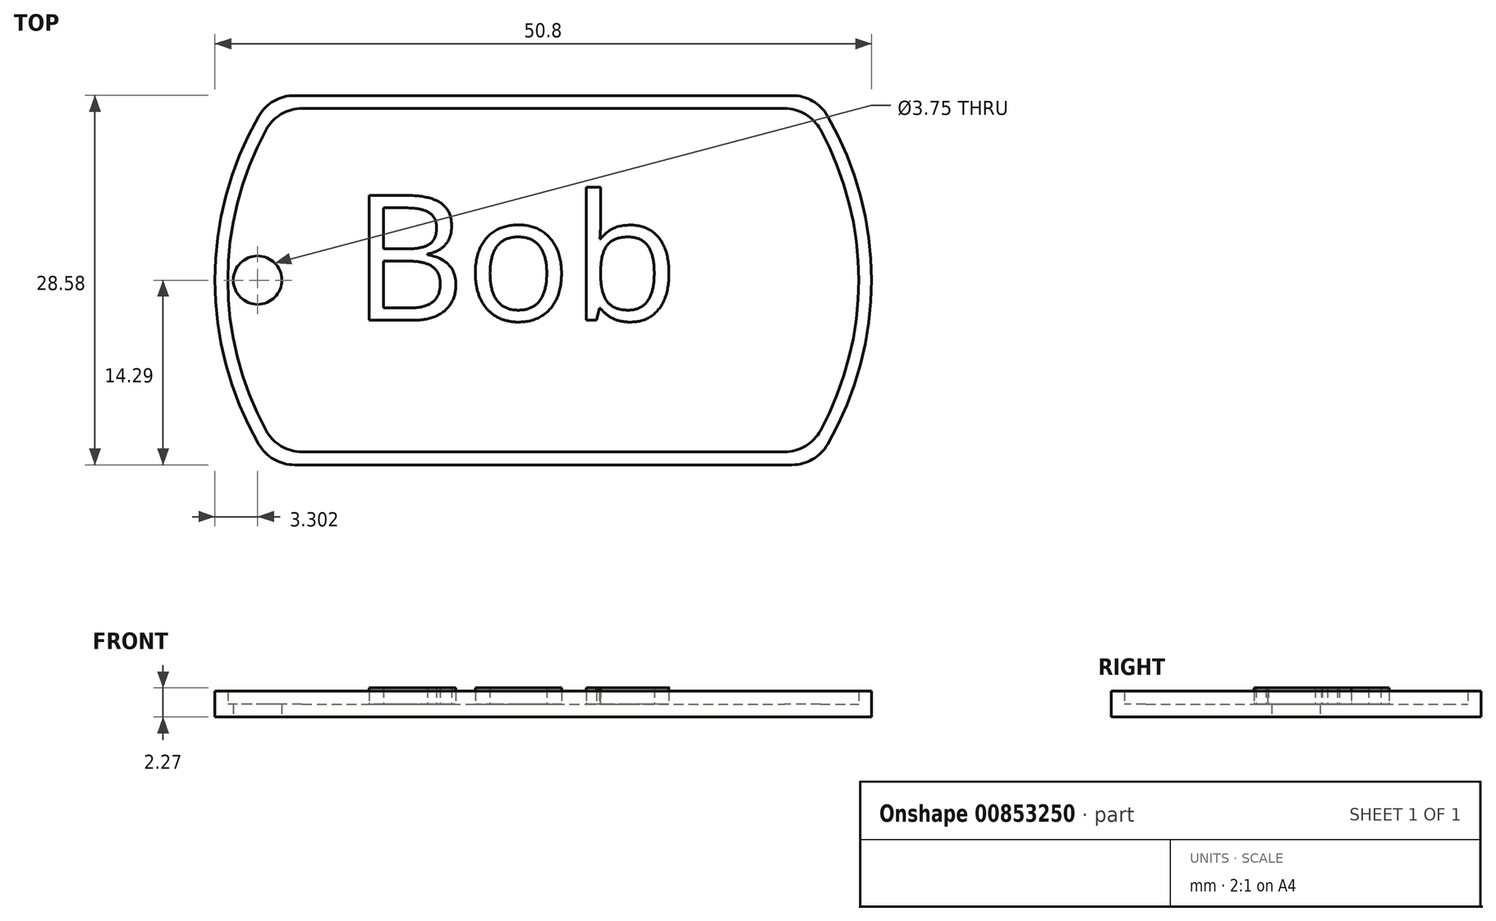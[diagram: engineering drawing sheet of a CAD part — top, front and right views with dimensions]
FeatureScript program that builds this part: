
annotation { "Feature Type Name" : "Feature", "Feature Type Description" : "" }
export const myFeature = defineFeature(function(context is Context, id is Id, definition is map)
    precondition{}
    {
        {
            var Q0;
            Q0=qCreatedBy(makeId("Top.planeOp"),FACE);
            var sketch = newSketch(context, id + "F0", { "sketchPlane" : qUnion([Q0])});
            skArc(sketch, "E0", {"start": v(-22, 12.7) * mm, "mid": v(-25.4, 0) * mm, "end": v(-22, -12.7) * mm});
            skLineSegment(sketch, "E1.top", {"start": v(-19.25, -14.29) * mm, "end": v(19.25, -14.29) * mm});
            skArc(sketch, "E2.trimOffspring", {"start": v(22, -12.7) * mm, "mid": v(25.4, 0) * mm, "end": v(22, 12.7) * mm});
            skLineSegment(sketch, "E3", {"start": v(-19.25, 14.29) * mm, "end": v(19.25, 14.29) * mm});
            skPoint(sketch, "E4.visualSharp", {"position": v(-21, 14.29) * mm});
            skArc(sketch, "E4.filletArc", {"start": v(-19.25, 14.29) * mm, "mid": v(-20.83, 13.86) * mm, "end": v(-22, 12.7) * mm});
            skPoint(sketch, "E5.visualSharp", {"position": v(21, 14.29) * mm});
            skArc(sketch, "E5.filletArc", {"start": v(22, 12.7) * mm, "mid": v(20.83, 13.86) * mm, "end": v(19.25, 14.29) * mm});
            skPoint(sketch, "E6.visualSharp", {"position": v(21, -14.29) * mm});
            skArc(sketch, "E6.filletArc", {"start": v(19.25, -14.29) * mm, "mid": v(20.83, -13.86) * mm, "end": v(22, -12.7) * mm});
            skPoint(sketch, "E7.visualSharp", {"position": v(-21, -14.29) * mm});
            skArc(sketch, "E7.filletArc", {"start": v(-22, -12.7) * mm, "mid": v(-20.83, -13.86) * mm, "end": v(-19.25, -14.29) * mm});
            skCircle(sketch, "E8", {"center": v(-22.1, 0) * mm, "radius": 1.87 * mm});
            skSolve(sketch);
        }
        {
            var Q0;
            Q0=makeQuery(id+"F0.imprint","IMPRINT",FACE,{"disambiguationData":[TD([[makeQuery(id+"F0.imprint","IMPRINT",EDGE,{"derivedFrom":sQuery(id+"F0.wireOp",EDGE,"E0")}),1.0]])]});
            extrude(context, id + "F1", {"entities" : qUnion([Q0]), "depth" : 1 * mm, "offsetDistance" : 25.4 * mm});
        }
        {
            var Q0;
            Q0=makeQuery(id+"F1.opExtrude","CAP_FACE",FACE,{"disambiguationData":[OSD([sQuery(id+"F0.wireOp",EDGE,"E0"),sQuery(id+"F0.wireOp",EDGE,"E1.top"),sQuery(id+"F0.wireOp",EDGE,"E2.trimOffspring"),sQuery(id+"F0.wireOp",EDGE,"E3"),sQuery(id+"F0.wireOp",EDGE,"E4.filletArc"),sQuery(id+"F0.wireOp",EDGE,"E5.filletArc"),sQuery(id+"F0.wireOp",EDGE,"E6.filletArc"),sQuery(id+"F0.wireOp",EDGE,"E7.filletArc")])],"isStart":false});
            var sketch = newSketch(context, id + "F2", { "sketchPlane" : qUnion([Q0])});
            skLineSegment(sketch, "E9.0", {"start": v(-18.66, 13.29) * mm, "end": v(18.66, 13.29) * mm});
            skArc(sketch, "E9.1", {"start": v(-21.45, 11.63) * mm, "mid": v(-24.4, 0) * mm, "end": v(-21.45, -11.63) * mm});
            skLineSegment(sketch, "E9.2", {"start": v(-18.66, -13.29) * mm, "end": v(18.66, -13.29) * mm});
            skArc(sketch, "E9.3", {"start": v(21.45, -11.63) * mm, "mid": v(24.4, 0) * mm, "end": v(21.45, 11.63) * mm});
            skPoint(sketch, "E10.visualSharp", {"position": v(-20.46, 13.29) * mm});
            skArc(sketch, "E10.filletArc", {"start": v(-18.66, 13.29) * mm, "mid": v(-20.29, 12.84) * mm, "end": v(-21.45, 11.63) * mm});
            skPoint(sketch, "E11.visualSharp", {"position": v(20.46, 13.29) * mm});
            skArc(sketch, "E11.filletArc", {"start": v(21.45, 11.63) * mm, "mid": v(20.29, 12.84) * mm, "end": v(18.66, 13.29) * mm});
            skPoint(sketch, "E12.visualSharp", {"position": v(20.46, -13.29) * mm});
            skArc(sketch, "E12.filletArc", {"start": v(18.66, -13.29) * mm, "mid": v(20.29, -12.84) * mm, "end": v(21.45, -11.63) * mm});
            skPoint(sketch, "E13.visualSharp", {"position": v(-20.46, -13.29) * mm});
            skArc(sketch, "E13.filletArc", {"start": v(-21.45, -11.63) * mm, "mid": v(-20.29, -12.84) * mm, "end": v(-18.66, -13.29) * mm});
            skLineSegment(sketch, "E14.0", {"start": v(-19.25, 14.29) * mm, "end": v(19.25, 14.29) * mm});
            skArc(sketch, "E14.1", {"start": v(-22, 12.7) * mm, "mid": v(-25.4, 0) * mm, "end": v(-22, -12.7) * mm});
            skLineSegment(sketch, "E14.2", {"start": v(-19.25, -14.29) * mm, "end": v(19.25, -14.29) * mm});
            skArc(sketch, "E14.3", {"start": v(22, -12.7) * mm, "mid": v(25.4, 0) * mm, "end": v(22, 12.7) * mm});
            skPoint(sketch, "E15.visualSharp", {"position": v(-21, -14.29) * mm});
            skArc(sketch, "E15.filletArc", {"start": v(-22, -12.7) * mm, "mid": v(-20.83, -13.86) * mm, "end": v(-19.25, -14.29) * mm});
            skPoint(sketch, "E16.visualSharp", {"position": v(21, -14.29) * mm});
            skArc(sketch, "E16.filletArc", {"start": v(19.25, -14.29) * mm, "mid": v(20.83, -13.86) * mm, "end": v(22, -12.7) * mm});
            skPoint(sketch, "E17.visualSharp", {"position": v(21, 14.29) * mm});
            skArc(sketch, "E17.filletArc", {"start": v(22, 12.7) * mm, "mid": v(20.83, 13.86) * mm, "end": v(19.25, 14.29) * mm});
            skPoint(sketch, "E18.visualSharp", {"position": v(-21, 14.29) * mm});
            skArc(sketch, "E18.filletArc", {"start": v(-19.25, 14.29) * mm, "mid": v(-20.83, 13.86) * mm, "end": v(-22, 12.7) * mm});
            skSolve(sketch);
        }
        {
            var Q0;
            Q0=makeQuery(id+"F2.imprint","IMPRINT",FACE,{"disambiguationData":[TD([[makeQuery(id+"F2.imprint","IMPRINT",EDGE,{"derivedFrom":sQuery(id+"F2.wireOp",EDGE,"E9.0")}),1.0]])]});
            extrude(context, id + "F3", {"entities" : qUnion([Q0]), "operationType" : NewBodyOperationType.ADD, "depth" : 1 * mm, "offsetDistance" : 25.4 * mm});
        }
        {
            var Q0;
            Q0=makeQuery(id+"F1.opExtrude","CAP_FACE",FACE,{"disambiguationData":[OSD([sQuery(id+"F0.wireOp",EDGE,"E0"),sQuery(id+"F0.wireOp",EDGE,"E1.top"),sQuery(id+"F0.wireOp",EDGE,"E2.trimOffspring"),sQuery(id+"F0.wireOp",EDGE,"E3"),sQuery(id+"F0.wireOp",EDGE,"E4.filletArc"),sQuery(id+"F0.wireOp",EDGE,"E5.filletArc"),sQuery(id+"F0.wireOp",EDGE,"E6.filletArc"),sQuery(id+"F0.wireOp",EDGE,"E7.filletArc"),sQuery(id+"F0.wireOp",EDGE,"E8")])],"isStart":false});
            var sketch = newSketch(context, id + "F4", { "sketchPlane" : qUnion([Q0])});
            skText(sketch, "E19", { "text": "Bob", "fontName": "OpenSans-Regular.ttf"});
            const initialGuessF4  = {"E19": [-0.0148, -0.00311, 1, 0, 0.00976]};
            skSetInitialGuess(sketch, initialGuessF4);
            skSolve(sketch);
        }
        {
            var Q0;
            Q0 = qSketchRegion(id + "F4", true);
            extrude(context, id + "F5", {"entities" : qUnion([Q0]), "operationType" : NewBodyOperationType.ADD, "depth" : 1.27 * mm, "offsetDistance" : 25.4 * mm});
        }
    });
